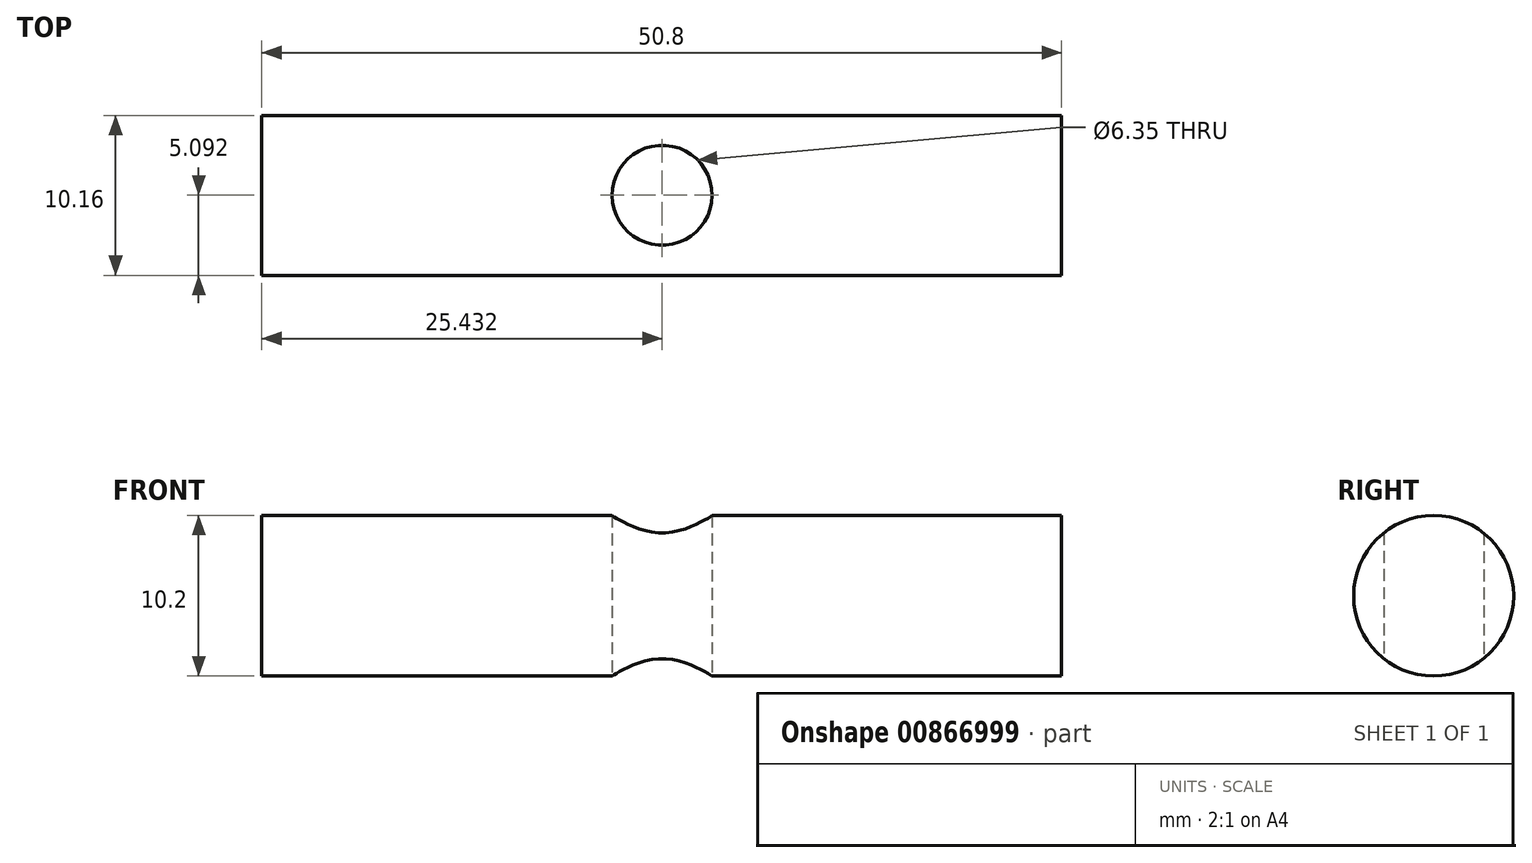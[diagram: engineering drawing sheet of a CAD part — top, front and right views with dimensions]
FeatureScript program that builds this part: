
annotation { "Feature Type Name" : "Feature", "Feature Type Description" : "" }
export const myFeature = defineFeature(function(context is Context, id is Id, definition is map)
    precondition{}
    {
        {
            var Q0;
            Q0=qCreatedBy(makeId("Front.planeOp"),FACE);
            var sketch = newSketch(context, id + "F0", { "sketchPlane" : qUnion([Q0])});
            skLineSegment(sketch, "E0", {"start": v(0, 0) * mm, "end": v(-25.4, 0) * mm});
            skLineSegment(sketch, "E1", {"start": v(-25.4, 0) * mm, "end": v(-25.4, 10.2) * mm});
            skLineSegment(sketch, "E2", {"start": v(-25.4, 10.2) * mm, "end": v(0, 10.2) * mm});
            skLineSegment(sketch, "E3", {"start": v(0, 10.2) * mm, "end": v(25.4, 10.2) * mm});
            skLineSegment(sketch, "E4", {"start": v(25.4, 10.2) * mm, "end": v(25.4, 0) * mm});
            skLineSegment(sketch, "E5", {"start": v(25.4, 0) * mm, "end": v(0, 0) * mm});
            skSolve(sketch);
        }
        {
            var Q0;
            Q0=makeQuery(id+"F0.imprint","IMPRINT",FACE,{"disambiguationData":[TD([[makeQuery(id+"F0.imprint","IMPRINT",EDGE,{"derivedFrom":sQuery(id+"F0.wireOp",EDGE,"E0")}),-1.0]])]});
            extrude(context, id + "F1", {"entities" : qUnion([Q0]), "depth" : 10.16 * mm, "offsetDistance" : 25.4 * mm});
        }
        {
            var Q0;
            Q0=qCreatedBy(makeId("Top.planeOp"),FACE);
            var sketch = newSketch(context, id + "F2", { "sketchPlane" : qUnion([Q0])});
            skCircle(sketch, "E6", {"center": v(0.03, -5.07) * mm, "radius": 5.07 * mm});
            skPoint(sketch, "E6.first.point", {"position": v(0, 0) * mm});
            skPoint(sketch, "E6.second.point", {"position": v(0, -10.14) * mm});
            skPoint(sketch, "E6.third.point", {"position": v(4.32, -7.77) * mm});
            skSolve(sketch);
        }
        {
            var Q0;
            Q0=sQuery(id+"F2.wireOp",VERTEX,"E6.center");
            var Q1;
            Q1=makeQuery(id+"F1.opExtrude","SWEPT_BODY",BODY,{"disambiguationData":[OSD([sQuery(id+"F0.wireOp",EDGE,"E0"),sQuery(id+"F0.wireOp",EDGE,"E1"),sQuery(id+"F0.wireOp",EDGE,"E2"),sQuery(id+"F0.wireOp",EDGE,"E3"),sQuery(id+"F0.wireOp",EDGE,"E4"),sQuery(id+"F0.wireOp",EDGE,"E5")])]});
            hole(context, id + "F3", {"style" : HoleStyle.SIMPLE, "endStyle" : HoleEndStyle.THROUGH, "oppositeDirection" : true, "holeDiameter" : 6.35 * mm, "majorDiameter" : 6.35 * mm, "isTappedThrough" : true, "tappedDepth" : 12.7 * mm, "tapClearance" : 3, "locations" : qUnion([Q0]), "scope" : qUnion([Q1])});
        }
        {
            var Q0;
            Q0=makeQuery(id+"F1.opExtrude","CAP_EDGE",EDGE,{"disambiguationData":[OSD([sQuery(id+"F0.wireOp",EDGE,"E2"),sQuery(id+"F0.wireOp",EDGE,"E3")])],"isStart":false});
            var Q1;
            Q1=makeQuery(id+"F1.opExtrude","CAP_EDGE",EDGE,{"disambiguationData":[OSD([sQuery(id+"F0.wireOp",EDGE,"E2"),sQuery(id+"F0.wireOp",EDGE,"E3")])],"isStart":true});
            var Q2;
            Q2=makeQuery(id+"F1.opExtrude","CAP_EDGE",EDGE,{"disambiguationData":[OSD([sQuery(id+"F0.wireOp",EDGE,"E0"),sQuery(id+"F0.wireOp",EDGE,"E5")])],"isStart":false});
            var Q3;
            Q3=makeQuery(id+"F1.opExtrude","CAP_EDGE",EDGE,{"disambiguationData":[OSD([sQuery(id+"F0.wireOp",EDGE,"E0"),sQuery(id+"F0.wireOp",EDGE,"E5")])],"isStart":true});
            fillet(context, id + "F4", {"entities" : qUnion([Q0, Q1, Q2, Q3]), "radius" : 5.08 * mm, "tangentPropagation" : true, "allowEdgeOverflow" : false});
        }
    });
